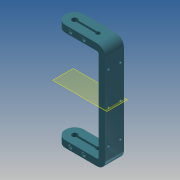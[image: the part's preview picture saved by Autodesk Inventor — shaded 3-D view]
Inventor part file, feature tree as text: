
AUTODESK INVENTOR PART (.ipt)
format: ipt  version: 2013 (Build 170138000, 138)  size: 259,072 bytes
history: native  units: mm
features: extrude x10, sketch x10, projected_geometry x2, fillet x1, pattern_linear x1, plane x1, mirror x1
ambient origin geometry x8: Origin, YZ Plane, XZ Plane, XY Plane, X Axis, Y Axis, Z Axis, Center Point
bodies: Solid1 (feature_tree)
feature tree (26):
  extrude  "Extrusion1"  Depth=28.0mm
  extrude  "Extrusion2"  Depth=160.0mm
  extrude  "Extrusion3"  Depth=10.0mm TaperAngle=0.0deg
  fillet  "Fillet2"  Radius=2.5mm
  extrude  "Extrusion11"  Depth=3.5mm
  extrude  "Extrusion12"  Depth=10.0mm TaperAngle=0.0deg
  pattern_linear  "Rectangular Pattern2"  Count1=3  [1 undecoded]
  extrude  "Extrusion17"  Depth=6.0mm
  extrude  "Extrusion18"  Depth=10.0mm TaperAngle=0.0deg
  extrude  "Extrusion19"  Depth=10.0mm TaperAngle=0.0deg
  extrude  "Extrusion20"  Depth=27.5mm
  extrude  "Extrusion21"  Depth=7.5mm
  plane  "Work Plane2"
  mirror  "Mirror1"
  sketch  "Sketch1"  dims[d0=60.0mm d2=28.0mm]
  sketch  "Sketch2"  dims[d3=10.0mm d4=0.0mm d5=160.0mm]
  sketch  "Sketch3"  dims[d6=10.0mm d7=0.0mm d8=10.0mm d9=0.0mm d41=2.5mm d42=12.5mm]
  projected_geometry  "Projected Loop1"
  sketch  "Sketch11"  dims[d49=20.0mm d50=3.5mm]
  projected_geometry  "Projected Loop2"
  sketch  "Sketch12"  dims[d51=18.0mm d52=10.0mm d53=0.0mm]
  sketch  "Sketch17"  dims[d54=5.5mm]
  sketch  "Sketch18"  dims[d55=4.0mm d56=0.0mm d76=30.0mm d78=50.0mm]
  sketch  "Sketch19"  dims[d79=8.0mm d81=6.0mm]
  sketch  "Sketch20"  dims[d82=35.0mm d83=10.0mm d84=0.0mm]
  sketch  "Sketch21"  dims[d85=3.0mm d87=10.0mm d88=0.0mm d89=27.5mm d90=7.5mm d91=3.5mm d92=10.0mm d93=0.0mm d94=6.0mm d96=3.0mm d97=0.0mm d98=5.5mm d99=4.0mm d100=0.0mm]
note: 1 required parameter value undecoded (feature->parameter linkage not recoverable at this tier; creation-order binding heuristic only, values carry confidence <= 0.55)
